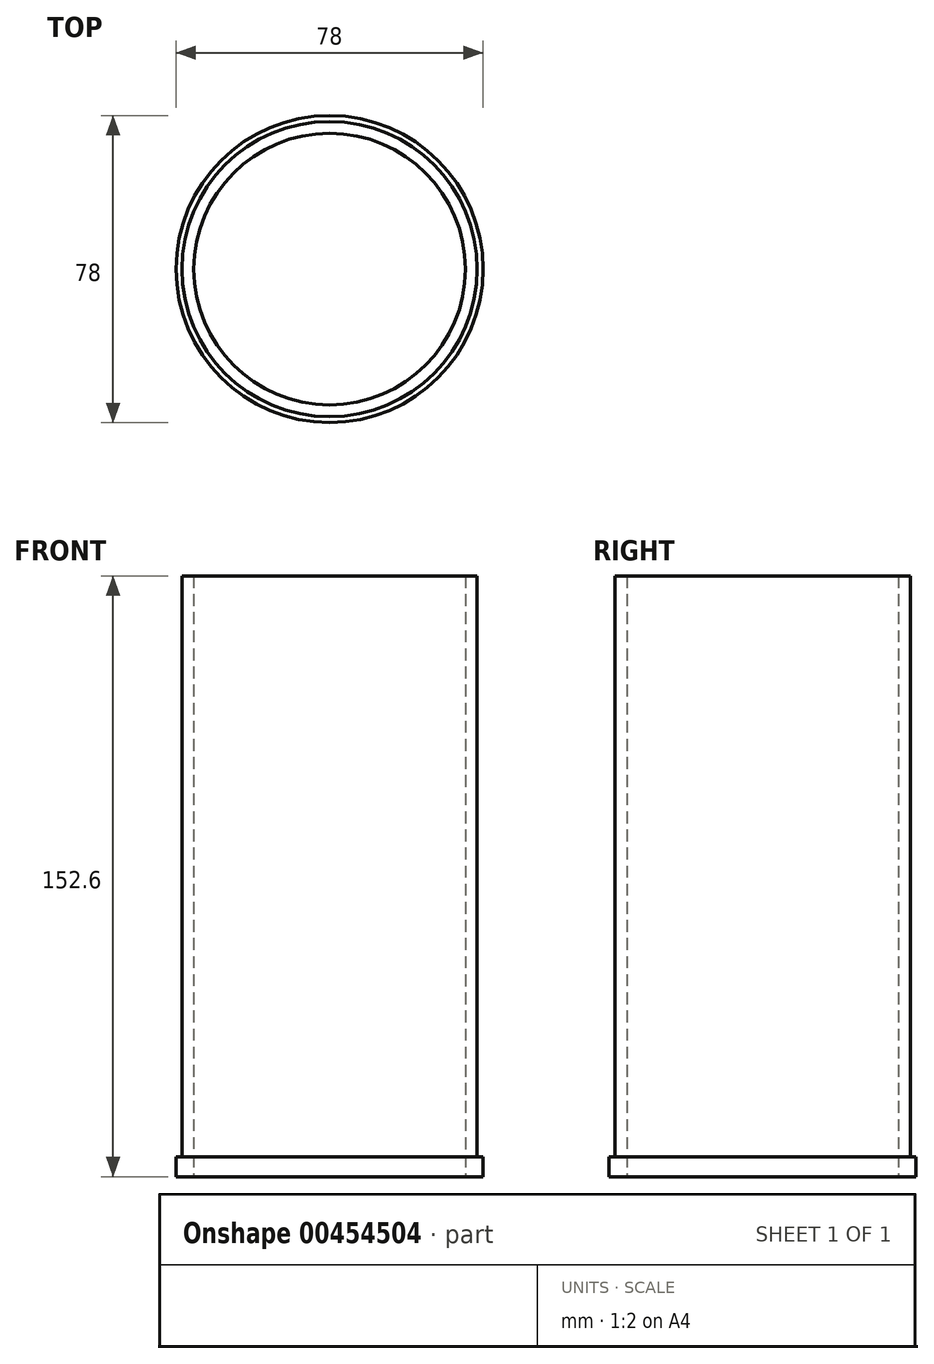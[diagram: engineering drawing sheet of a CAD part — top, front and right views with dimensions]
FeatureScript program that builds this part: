
annotation { "Feature Type Name" : "Feature", "Feature Type Description" : "" }
export const myFeature = defineFeature(function(context is Context, id is Id, definition is map)
    precondition{}
    {
        {
            var Q0;
            Q0=qCreatedBy(makeId("Top.planeOp"),FACE);
            var sketch = newSketch(context, id + "F0", { "sketchPlane" : qUnion([Q0])});
            skCircle(sketch, "E0", {"center": v(0, 0) * mm, "radius": 37.5 * mm});
            skSolve(sketch);
        }
        {
            var Q0;
            Q0 = qSketchRegion(id + "F0", true);
            extrude(context, id + "F1", {"entities" : qUnion([Q0]), "depth" : 152.6 * mm});
        }
        {
            var Q0;
            Q0=makeQuery(id+"F1.opExtrude","CAP_FACE",FACE,{"disambiguationData":[OSD([sQuery(id+"F0.wireOp",EDGE,"E0")])],"isStart":false});
            var Q1;
            Q1=makeQuery(id+"F1.opExtrude","CAP_FACE",FACE,{"disambiguationData":[OSD([sQuery(id+"F0.wireOp",EDGE,"E0")])],"isStart":true});
            shell(context, id + "F2", {"entities" : qUnion([Q0, Q1]), "thickness" : 3 * mm});
        }
        {
            var Q0;
            Q0=qCreatedBy(makeId("Top.planeOp"),FACE);
            cPlane(context, id + "F3", {"entities" : qUnion([Q0]), "cplaneType" : CPlaneType.OFFSET, "offset" : 152.6 * mm, "width" : 150 * mm, "height" : 150 * mm});
        }
        {
            var Q0;
            Q0=qCreatedBy(makeId("Top.planeOp"),FACE);
            var sketch = newSketch(context, id + "F4", { "sketchPlane" : qUnion([Q0])});
            skCircle(sketch, "E1", {"center": v(0, 0) * mm, "radius": 37.5 * mm});
            skCircle(sketch, "E2", {"center": v(0, 0) * mm, "radius": 39 * mm});
            skSolve(sketch);
        }
        {
            var Q0;
            Q0=makeQuery(id+"F4.imprint","IMPRINT",FACE,{"disambiguationData":[TD([[makeQuery(id+"F4.imprint","IMPRINT",EDGE,{"derivedFrom":sQuery(id+"F4.wireOp",EDGE,"E1")}),-1.0]])]});
            extrude(context, id + "F5", {"entities" : qUnion([Q0]), "operationType" : NewBodyOperationType.ADD, "depth" : 5 * mm});
        }
    });
